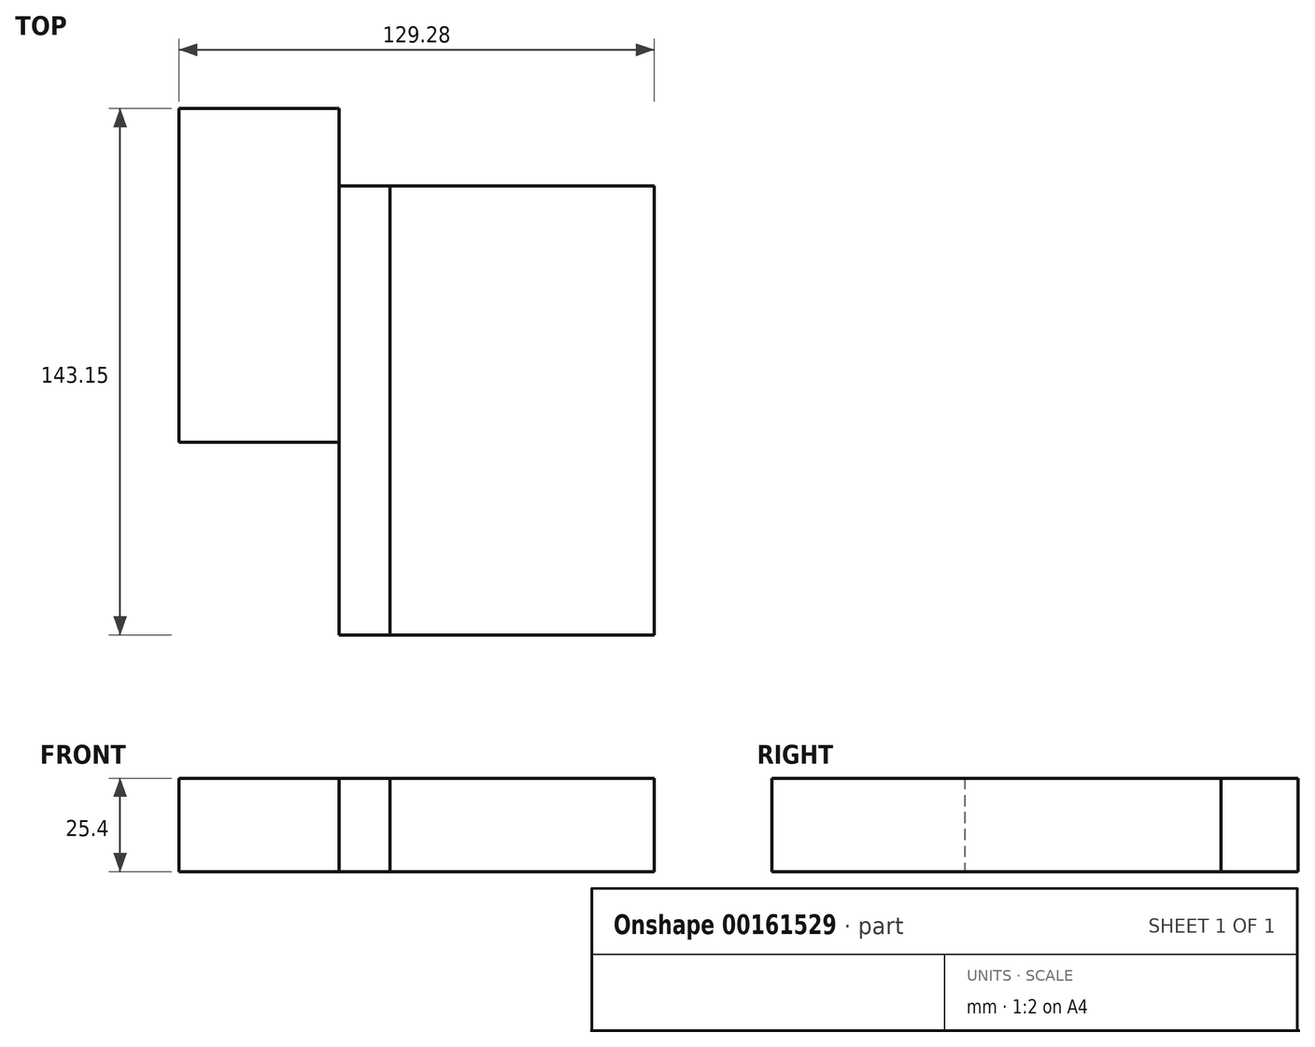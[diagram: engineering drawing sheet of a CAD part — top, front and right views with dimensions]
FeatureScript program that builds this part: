
annotation { "Feature Type Name" : "Feature", "Feature Type Description" : "" }
export const myFeature = defineFeature(function(context is Context, id is Id, definition is map)
    precondition{}
    {
        {
            var Q0;
            Q0=qCreatedBy(makeId("Top.planeOp"),FACE);
            var sketch = newSketch(context, id + "F0", { "sketchPlane" : qUnion([Q0])});
            skLineSegment(sketch, "E0.bottom", {"start": v(-93.33, -8.62) * mm, "end": v(-49.75, -8.62) * mm});
            skLineSegment(sketch, "E0.top", {"start": v(-93.33, 82.08) * mm, "end": v(-49.75, 82.08) * mm});
            skLineSegment(sketch, "E0.left", {"start": v(-93.33, -8.62) * mm, "end": v(-93.33, 82.08) * mm});
            skLineSegment(sketch, "E0.right", {"start": v(-49.75, -8.62) * mm, "end": v(-49.75, 82.08) * mm});
            skPoint(sketch, "E0.middle", {"position": v(-71.54, 36.73) * mm});
            skLineSegment(sketch, "E1.bottom", {"start": v(35.95, 61.07) * mm, "end": v(-35.95, 61.07) * mm});
            skLineSegment(sketch, "E1.top", {"start": v(35.95, -61.07) * mm, "end": v(-35.95, -61.07) * mm});
            skLineSegment(sketch, "E1.left", {"start": v(35.95, 61.07) * mm, "end": v(35.95, -61.07) * mm});
            skLineSegment(sketch, "E1.right", {"start": v(-35.95, 61.07) * mm, "end": v(-35.95, -61.07) * mm});
            skPoint(sketch, "E1.middle", {"position": v(0, 0) * mm});
            skSolve(sketch);
        }
        {
            var Q0;
            Q0=makeQuery(id+"F0.imprint","IMPRINT",FACE,{"disambiguationData":[TD([[makeQuery(id+"F0.imprint","IMPRINT",EDGE,{"derivedFrom":sQuery(id+"F0.wireOp",EDGE,"E0.bottom")}),1.0]])]});
            var Q1;
            Q1=makeQuery(id+"F0.imprint","IMPRINT",FACE,{"disambiguationData":[TD([[makeQuery(id+"F0.imprint","IMPRINT",EDGE,{"derivedFrom":sQuery(id+"F0.wireOp",EDGE,"E1.bottom")}),1.0]])]});
            extrude(context, id + "F1", {"entities" : qUnion([Q0, Q1]), "depth" : 25.4 * mm});
        }
        {
            var Q0;
            Q0=makeQuery(id+"F1.opExtrude","SWEPT_FACE",FACE,{"disambiguationData":[OSD([sQuery(id+"F0.wireOp",EDGE,"E1.right")])]});
            var Q1;
            Q1=makeQuery(id+"F1.opExtrude","SWEPT_FACE",FACE,{"disambiguationData":[OSD([sQuery(id+"F0.wireOp",EDGE,"E0.right")])]});
            extrude(context, id + "F2", {"entities" : qUnion([Q0]), "endBound" : BoundingType.UP_TO_SURFACE, "endBoundEntityFace" : qUnion([Q1]), "depth" : 25.4 * mm});
        }
    });
